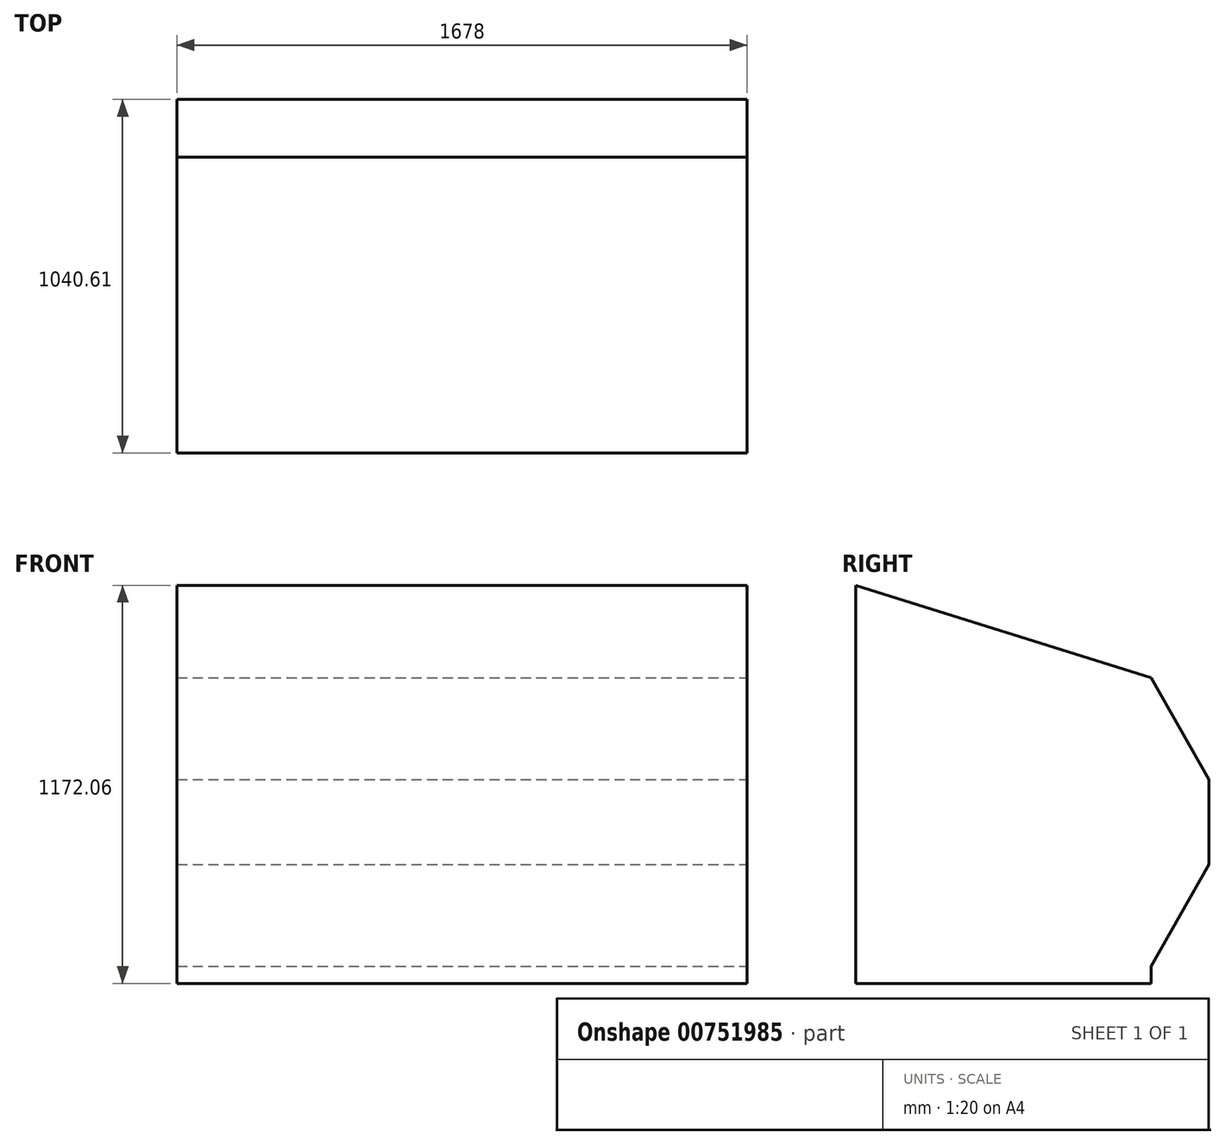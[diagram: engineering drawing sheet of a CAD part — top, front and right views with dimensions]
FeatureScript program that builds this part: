
annotation { "Feature Type Name" : "Feature", "Feature Type Description" : "" }
export const myFeature = defineFeature(function(context is Context, id is Id, definition is map)
    precondition{}
    {
        {
            var Q0;
            Q0=qCreatedBy(makeId("Right.planeOp"),FACE);
            var sketch = newSketch(context, id + "F0", { "sketchPlane" : qUnion([Q0])});
            skLineSegment(sketch, "E0", {"start": v(0, 0) * mm, "end": v(0, 25) * mm});
            skLineSegment(sketch, "E1", {"start": v(0, 25) * mm, "end": v(170, 325) * mm});
            skLineSegment(sketch, "E2", {"start": v(170, 325) * mm, "end": v(170, 575) * mm});
            skLineSegment(sketch, "E3", {"start": v(170, 575) * mm, "end": v(0, 875) * mm});
            skLineSegment(sketch, "E4", {"start": v(0, 875) * mm, "end": v(820, 618.75) * mm});
            skPoint(sketch, "E5.orphan", {"position": v(800, 625) * mm});
            skPoint(sketch, "E6.orphan", {"position": v(920, 0) * mm});
            skLineSegment(sketch, "E7", {"start": v(820, 618.75) * mm, "end": v(597.7, -25) * mm});
            skPoint(sketch, "E8.end.orphan", {"position": v(920, 575) * mm});
            skLineSegment(sketch, "E9", {"start": v(0, 0) * mm, "end": v(0, -25) * mm});
            skLineSegment(sketch, "E10", {"start": v(0, -25) * mm, "end": v(597.7, -25) * mm});
            skPoint(sketch, "E11.start.orphan", {"position": v(606.34, 0) * mm});
            skSolve(sketch);
        }
        {
            var Q0;
            Q0=makeQuery(id+"F0.imprint","IMPRINT",FACE,{"disambiguationData":[TD([[makeQuery(id+"F0.imprint","IMPRINT",EDGE,{"derivedFrom":sQuery(id+"F0.wireOp",EDGE,"E0")}),-1.0]])]});
            extrude(context, id + "F1", {"entities" : qUnion([Q0]), "depth" : 1678 * mm, "offsetDistance" : 25 * mm, "symmetric" : true});
        }
        {
            var Q0;
            Q0=makeQuery(id+"F1.opExtrude","CAP_FACE",FACE,{"disambiguationData":[OSD([sQuery(id+"F0.wireOp",EDGE,"E0"),sQuery(id+"F0.wireOp",EDGE,"E1"),sQuery(id+"F0.wireOp",EDGE,"E2"),sQuery(id+"F0.wireOp",EDGE,"E3"),sQuery(id+"F0.wireOp",EDGE,"E11"),sQuery(id+"F0.wireOp",EDGE,"E4"),sQuery(id+"F0.wireOp",EDGE,"E7")])],"isStart":false});
            var sketch = newSketch(context, id + "F2", { "sketchPlane" : qUnion([Q0])});
            skLineSegment(sketch, "E12", {"start": v(0, 875) * mm, "end": v(-870.6, 1147.06) * mm});
            skLineSegment(sketch, "E13", {"start": v(-870.6, -25) * mm, "end": v(-870.6, 1147.06) * mm});
            skPoint(sketch, "E14.0.2.start.orphan", {"position": v(0, 875) * mm});
            skPoint(sketch, "E14.0.3.start.orphan", {"position": v(170, 575) * mm});
            skPoint(sketch, "E15.0.end.orphan", {"position": v(170, 325) * mm});
            skPoint(sketch, "E14.0.0.end.orphan", {"position": v(820, 618.75) * mm});
            skPoint(sketch, "E14.0.6.end.orphan", {"position": v(820, 618.75) * mm});
            skPoint(sketch, "E14.0.5.end.orphan", {"position": v(0, 25) * mm});
            skPoint(sketch, "E14.0.5.start.orphan", {"position": v(0, 25) * mm});
            skLineSegment(sketch, "E16.0", {"start": v(170, 575) * mm, "end": v(0, 875) * mm});
            skLineSegment(sketch, "E17.0", {"start": v(170, 325) * mm, "end": v(170, 575) * mm});
            skLineSegment(sketch, "E18.0", {"start": v(0, 25) * mm, "end": v(170, 325) * mm});
            skLineSegment(sketch, "E19.0", {"start": v(0, 0) * mm, "end": v(0, 25) * mm});
            skPoint(sketch, "E20.0", {"position": v(0, -12.5) * mm});
            skLineSegment(sketch, "E21.0", {"start": v(0, 0) * mm, "end": v(0, -25) * mm});
            skLineSegment(sketch, "E22", {"start": v(0, -25) * mm, "end": v(-870.6, -25) * mm});
            skSolve(sketch);
        }
        {
            var Q0;
            Q0 = qSketchRegion(id + "F2", true);
            extrude(context, id + "F3", {"entities" : qUnion([Q0]), "oppositeDirection" : true, "depth" : 1678 * mm, "offsetDistance" : 25 * mm});
        }
        {
            var Q0;
            Q0=makeQuery(id+"F1.opExtrude","SWEPT_BODY",BODY,{"disambiguationData":[OSD([sQuery(id+"F0.wireOp",EDGE,"E0"),sQuery(id+"F0.wireOp",EDGE,"E1"),sQuery(id+"F0.wireOp",EDGE,"E2"),sQuery(id+"F0.wireOp",EDGE,"E3"),sQuery(id+"F0.wireOp",EDGE,"E4"),sQuery(id+"F0.wireOp",EDGE,"E7"),sQuery(id+"F0.wireOp",EDGE,"E9"),sQuery(id+"F0.wireOp",EDGE,"E10")])]});
            deleteBodies(context, id + "F4", {"entities" : qUnion([Q0])});
        }
    });
